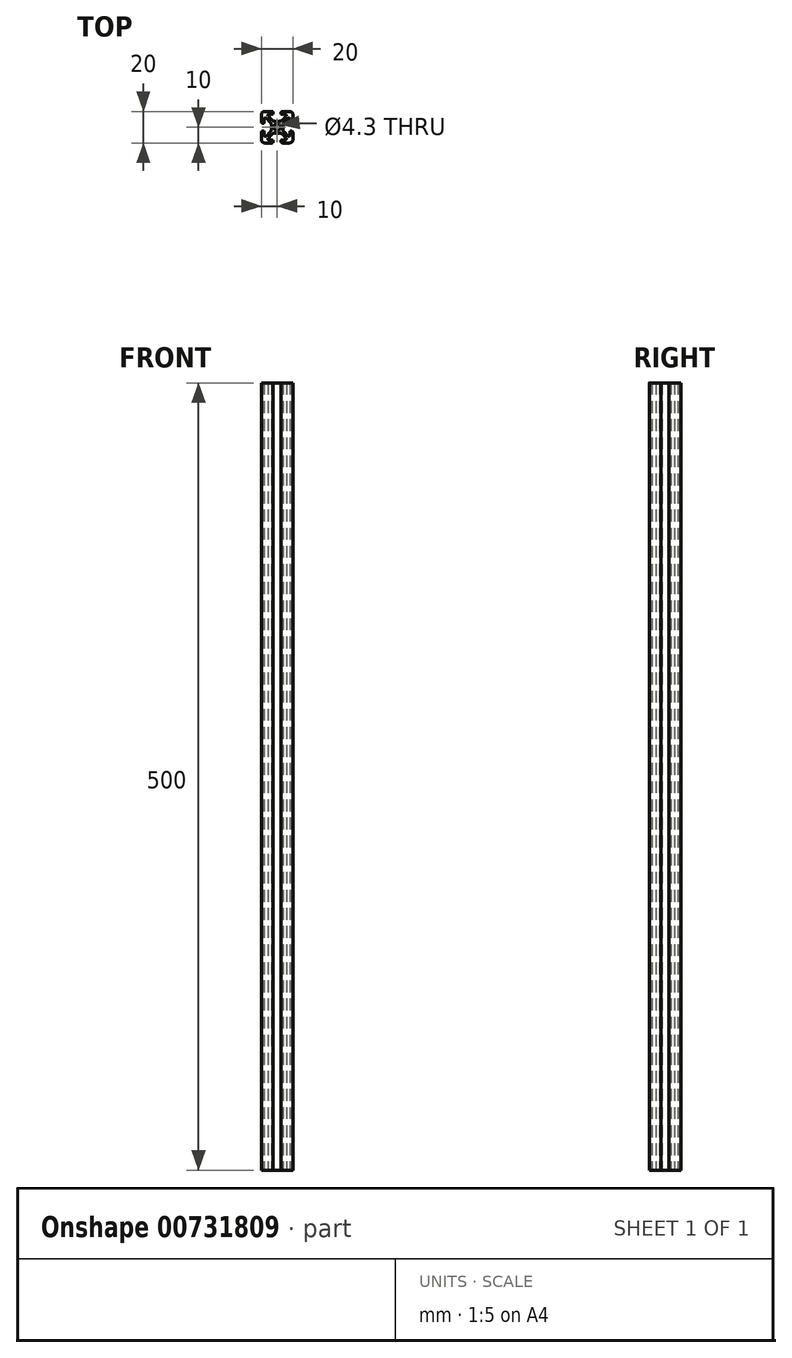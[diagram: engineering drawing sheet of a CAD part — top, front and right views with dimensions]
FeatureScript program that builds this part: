
annotation { "Feature Type Name" : "Feature", "Feature Type Description" : "" }
export const myFeature = defineFeature(function(context is Context, id is Id, definition is map)
    precondition{}
    {
        {
            var Q0;
            Q0=qCreatedBy(makeId("Top.planeOp"),FACE);
            var sketch = newSketch(context, id + "F0", { "sketchPlane" : qUnion([Q0])});
            skLineSegment(sketch, "E0.0.0", {"start": v(3.65, -1.13) * mm, "end": v(3.65, 1.13) * mm});
            skArc(sketch, "E0.0.1", {"start": v(3.65, 1.13) * mm, "mid": v(3.88, 2.28) * mm, "end": v(4.53, 3.26) * mm});
            skLineSegment(sketch, "E0.0.2", {"start": v(4.53, 3.26) * mm, "end": v(6.87, 5.6) * mm});
            skArc(sketch, "E0.0.3", {"start": v(6.87, 5.6) * mm, "mid": v(7.72, 5.76) * mm, "end": v(8.2, 5.04) * mm});
            skLineSegment(sketch, "E0.0.4", {"start": v(8.2, 5.04) * mm, "end": v(8.2, 2.87) * mm});
            skArc(sketch, "E0.0.5", {"start": v(8.5, 2.58) * mm, "mid": v(8.29, 2.66) * mm, "end": v(8.2, 2.87) * mm});
            skLineSegment(sketch, "E0.0.6", {"start": v(8.5, 2.58) * mm, "end": v(9.2, 2.58) * mm});
            skArc(sketch, "E0.0.7", {"start": v(10, 3.37) * mm, "mid": v(9.77, 2.8) * mm, "end": v(9.2, 2.58) * mm});
            skLineSegment(sketch, "E0.0.8", {"start": v(10, 3.37) * mm, "end": v(10, 8) * mm});
            skArc(sketch, "E0.0.9", {"start": v(8, 10) * mm, "mid": v(9.41, 9.41) * mm, "end": v(10, 8) * mm});
            skLineSegment(sketch, "E0.0.10", {"start": v(8, 10) * mm, "end": v(3.37, 10) * mm});
            skArc(sketch, "E0.0.11", {"start": v(2.57, 9.2) * mm, "mid": v(2.8, 9.77) * mm, "end": v(3.37, 10) * mm});
            skLineSegment(sketch, "E0.0.12", {"start": v(2.57, 9.2) * mm, "end": v(2.57, 8.5) * mm});
            skArc(sketch, "E0.0.13", {"start": v(2.87, 8.2) * mm, "mid": v(2.66, 8.29) * mm, "end": v(2.57, 8.5) * mm});
            skLineSegment(sketch, "E0.0.14", {"start": v(2.87, 8.2) * mm, "end": v(5.04, 8.2) * mm});
            skArc(sketch, "E0.0.15", {"start": v(5.04, 8.2) * mm, "mid": v(5.76, 7.72) * mm, "end": v(5.6, 6.87) * mm});
            skLineSegment(sketch, "E0.0.16", {"start": v(5.6, 6.87) * mm, "end": v(3.26, 4.53) * mm});
            skArc(sketch, "E0.0.17", {"start": v(3.26, 4.53) * mm, "mid": v(2.28, 3.88) * mm, "end": v(1.13, 3.65) * mm});
            skLineSegment(sketch, "E0.0.18", {"start": v(1.13, 3.65) * mm, "end": v(-1.13, 3.65) * mm});
            skArc(sketch, "E0.0.19", {"start": v(-1.13, 3.65) * mm, "mid": v(-2.28, 3.88) * mm, "end": v(-3.26, 4.53) * mm});
            skLineSegment(sketch, "E0.0.20", {"start": v(-3.26, 4.53) * mm, "end": v(-5.6, 6.87) * mm});
            skArc(sketch, "E0.0.21", {"start": v(-5.6, 6.87) * mm, "mid": v(-5.76, 7.72) * mm, "end": v(-5.04, 8.2) * mm});
            skLineSegment(sketch, "E0.0.22", {"start": v(-5.04, 8.2) * mm, "end": v(-2.87, 8.2) * mm});
            skArc(sketch, "E0.0.23", {"start": v(-2.57, 8.5) * mm, "mid": v(-2.66, 8.29) * mm, "end": v(-2.87, 8.2) * mm});
            skLineSegment(sketch, "E0.0.24", {"start": v(-2.57, 8.5) * mm, "end": v(-2.57, 9.2) * mm});
            skArc(sketch, "E0.0.25", {"start": v(-3.38, 10) * mm, "mid": v(-2.8, 9.77) * mm, "end": v(-2.57, 9.2) * mm});
            skLineSegment(sketch, "E0.0.26", {"start": v(-3.38, 10) * mm, "end": v(-8, 10) * mm});
            skArc(sketch, "E0.0.27", {"start": v(-10, 8) * mm, "mid": v(-9.41, 9.41) * mm, "end": v(-8, 10) * mm});
            skLineSegment(sketch, "E0.0.28", {"start": v(-10, 8) * mm, "end": v(-10, 3.37) * mm});
            skArc(sketch, "E0.0.29", {"start": v(-9.2, 2.58) * mm, "mid": v(-9.77, 2.8) * mm, "end": v(-10, 3.37) * mm});
            skLineSegment(sketch, "E0.0.30", {"start": v(-9.2, 2.58) * mm, "end": v(-8.5, 2.58) * mm});
            skArc(sketch, "E0.0.31", {"start": v(-8.2, 2.87) * mm, "mid": v(-8.29, 2.66) * mm, "end": v(-8.5, 2.58) * mm});
            skLineSegment(sketch, "E0.0.32", {"start": v(-8.2, 2.87) * mm, "end": v(-8.2, 5.04) * mm});
            skArc(sketch, "E0.0.33", {"start": v(-8.2, 5.04) * mm, "mid": v(-7.72, 5.76) * mm, "end": v(-6.87, 5.6) * mm});
            skLineSegment(sketch, "E0.0.34", {"start": v(-6.87, 5.6) * mm, "end": v(-4.53, 3.26) * mm});
            skArc(sketch, "E0.0.35", {"start": v(-4.53, 3.26) * mm, "mid": v(-3.88, 2.28) * mm, "end": v(-3.65, 1.13) * mm});
            skLineSegment(sketch, "E0.0.36", {"start": v(-3.65, 1.13) * mm, "end": v(-3.65, -1.13) * mm});
            skArc(sketch, "E0.0.37", {"start": v(-3.65, -1.13) * mm, "mid": v(-3.88, -2.28) * mm, "end": v(-4.53, -3.26) * mm});
            skLineSegment(sketch, "E0.0.38", {"start": v(-4.53, -3.26) * mm, "end": v(-6.87, -5.6) * mm});
            skArc(sketch, "E0.0.39", {"start": v(-6.87, -5.6) * mm, "mid": v(-7.72, -5.76) * mm, "end": v(-8.2, -5.04) * mm});
            skLineSegment(sketch, "E0.0.40", {"start": v(-8.2, -5.04) * mm, "end": v(-8.2, -2.87) * mm});
            skArc(sketch, "E0.0.41", {"start": v(-8.5, -2.57) * mm, "mid": v(-8.29, -2.66) * mm, "end": v(-8.2, -2.87) * mm});
            skLineSegment(sketch, "E0.0.42", {"start": v(-8.5, -2.57) * mm, "end": v(-9.2, -2.57) * mm});
            skArc(sketch, "E0.0.43", {"start": v(-10, -3.38) * mm, "mid": v(-9.77, -2.8) * mm, "end": v(-9.2, -2.57) * mm});
            skLineSegment(sketch, "E0.0.44", {"start": v(-10, -3.38) * mm, "end": v(-10, -8) * mm});
            skArc(sketch, "E0.0.45", {"start": v(-8, -10) * mm, "mid": v(-9.41, -9.41) * mm, "end": v(-10, -8) * mm});
            skLineSegment(sketch, "E0.0.46", {"start": v(-8, -10) * mm, "end": v(-3.38, -10) * mm});
            skArc(sketch, "E0.0.47", {"start": v(-2.58, -9.2) * mm, "mid": v(-2.8, -9.77) * mm, "end": v(-3.38, -10) * mm});
            skLineSegment(sketch, "E0.0.48", {"start": v(-2.58, -9.2) * mm, "end": v(-2.57, -8.5) * mm});
            skArc(sketch, "E0.0.49", {"start": v(-2.87, -8.2) * mm, "mid": v(-2.66, -8.29) * mm, "end": v(-2.57, -8.5) * mm});
            skLineSegment(sketch, "E0.0.50", {"start": v(-2.87, -8.2) * mm, "end": v(-5.04, -8.2) * mm});
            skArc(sketch, "E0.0.51", {"start": v(-5.04, -8.2) * mm, "mid": v(-5.76, -7.72) * mm, "end": v(-5.6, -6.87) * mm});
            skLineSegment(sketch, "E0.0.52", {"start": v(-5.6, -6.87) * mm, "end": v(-3.26, -4.53) * mm});
            skArc(sketch, "E0.0.53", {"start": v(-3.26, -4.53) * mm, "mid": v(-2.28, -3.88) * mm, "end": v(-1.13, -3.65) * mm});
            skLineSegment(sketch, "E0.0.54", {"start": v(-1.13, -3.65) * mm, "end": v(1.13, -3.65) * mm});
            skArc(sketch, "E0.0.55", {"start": v(1.13, -3.65) * mm, "mid": v(2.28, -3.88) * mm, "end": v(3.26, -4.53) * mm});
            skLineSegment(sketch, "E0.0.56", {"start": v(3.26, -4.53) * mm, "end": v(5.6, -6.87) * mm});
            skArc(sketch, "E0.0.57", {"start": v(5.6, -6.87) * mm, "mid": v(5.76, -7.72) * mm, "end": v(5.04, -8.2) * mm});
            skLineSegment(sketch, "E0.0.58", {"start": v(5.04, -8.2) * mm, "end": v(2.87, -8.2) * mm});
            skArc(sketch, "E0.0.59", {"start": v(2.57, -8.5) * mm, "mid": v(2.66, -8.29) * mm, "end": v(2.87, -8.2) * mm});
            skLineSegment(sketch, "E0.0.60", {"start": v(2.57, -8.5) * mm, "end": v(2.57, -9.2) * mm});
            skArc(sketch, "E0.0.61", {"start": v(3.37, -10) * mm, "mid": v(2.8, -9.77) * mm, "end": v(2.57, -9.2) * mm});
            skLineSegment(sketch, "E0.0.62", {"start": v(3.37, -10) * mm, "end": v(8, -10) * mm});
            skArc(sketch, "E0.0.63", {"start": v(10, -8) * mm, "mid": v(9.41, -9.41) * mm, "end": v(8, -10) * mm});
            skLineSegment(sketch, "E0.0.64", {"start": v(10, -8) * mm, "end": v(10, -3.38) * mm});
            skArc(sketch, "E0.0.65", {"start": v(9.2, -2.57) * mm, "mid": v(9.77, -2.8) * mm, "end": v(10, -3.38) * mm});
            skLineSegment(sketch, "E0.0.66", {"start": v(9.2, -2.57) * mm, "end": v(8.5, -2.57) * mm});
            skArc(sketch, "E0.0.67", {"start": v(8.2, -2.87) * mm, "mid": v(8.29, -2.66) * mm, "end": v(8.5, -2.57) * mm});
            skLineSegment(sketch, "E0.0.68", {"start": v(8.2, -2.87) * mm, "end": v(8.2, -5.04) * mm});
            skArc(sketch, "E0.0.69", {"start": v(8.2, -5.04) * mm, "mid": v(7.72, -5.76) * mm, "end": v(6.87, -5.6) * mm});
            skLineSegment(sketch, "E0.0.70", {"start": v(6.87, -5.6) * mm, "end": v(4.53, -3.26) * mm});
            skArc(sketch, "E0.0.71", {"start": v(4.53, -3.26) * mm, "mid": v(3.88, -2.28) * mm, "end": v(3.65, -1.13) * mm});
            skSolve(sketch);
        }
        {
            var Q0;
            Q0 = qSketchRegion(id + "F0", true);
            extrude(context, id + "F1", {"entities" : qUnion([Q0]), "depth" : 500 * mm, "offsetDistance" : 25 * mm});
        }
        {
            var Q0;
            Q0=qCreatedBy(makeId("Top.planeOp"),FACE);
            var sketch = newSketch(context, id + "F2", { "sketchPlane" : qUnion([Q0])});
            skCircle(sketch, "E1", {"center": v(0, 0) * mm, "radius": 2.15 * mm});
            skSolve(sketch);
        }
        {
            var Q0;
            Q0 = qSketchRegion(id + "F2", true);
            extrude(context, id + "F3", {"entities" : qUnion([Q0]), "operationType" : NewBodyOperationType.REMOVE, "endBound" : BoundingType.UP_TO_NEXT, "depth" : 25 * mm, "offsetDistance" : 25 * mm});
        }
    });
